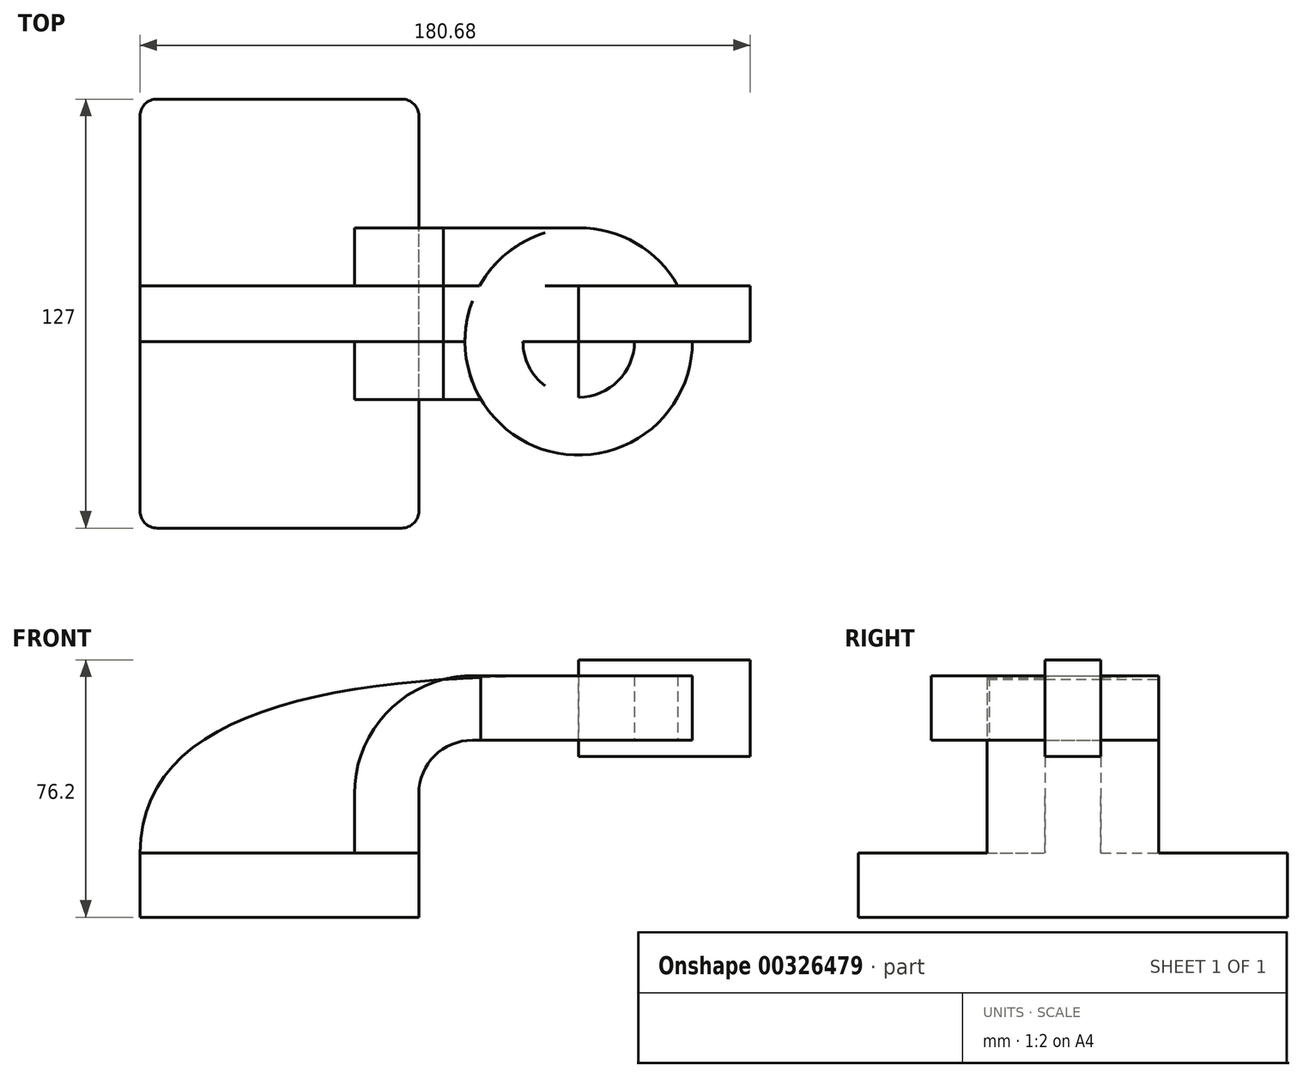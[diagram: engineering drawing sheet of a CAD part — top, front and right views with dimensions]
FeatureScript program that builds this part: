
annotation { "Feature Type Name" : "Feature", "Feature Type Description" : "" }
export const myFeature = defineFeature(function(context is Context, id is Id, definition is map)
    precondition{}
    {
        {
            var Q0;
            Q0=qCreatedBy(makeId("Front.planeOp"),FACE);
            var sketch = newSketch(context, id + "F0", { "sketchPlane" : qUnion([Q0])});
            skLineSegment(sketch, "E0.bottom", {"start": v(-41.28, 9.52) * mm, "end": v(41.27, 9.53) * mm});
            skLineSegment(sketch, "E0.top", {"start": v(-41.28, -9.52) * mm, "end": v(41.28, -9.52) * mm});
            skLineSegment(sketch, "E0.left", {"start": v(-41.28, 9.52) * mm, "end": v(-41.28, -9.53) * mm});
            skLineSegment(sketch, "E0.right", {"start": v(41.27, 9.53) * mm, "end": v(41.28, -9.52) * mm});
            skPoint(sketch, "E0.middle", {"position": v(0, 0) * mm});
            skLineSegment(sketch, "E1.bottom", {"start": v(88.6, 38.1) * mm, "end": v(139.4, 38.1) * mm});
            skLineSegment(sketch, "E1.top", {"start": v(88.6, 66.68) * mm, "end": v(139.4, 66.68) * mm});
            skLineSegment(sketch, "E1.left", {"start": v(88.6, 38.1) * mm, "end": v(88.6, 66.68) * mm});
            skLineSegment(sketch, "E1.right", {"start": v(139.4, 38.1) * mm, "end": v(139.4, 66.68) * mm});
            skPoint(sketch, "E1.middle", {"position": v(114, 52.39) * mm});
            skLineSegment(sketch, "E2", {"start": v(41.27, 9.53) * mm, "end": v(41.27, 27) * mm});
            skArc(sketch, "E3", {"start": v(41.27, 27) * mm, "mid": v(45.92, 38.23) * mm, "end": v(57.15, 42.88) * mm});
            skLineSegment(sketch, "E4", {"start": v(57.15, 42.88) * mm, "end": v(113.89, 42.88) * mm});
            skLineSegment(sketch, "E5.0", {"start": v(57.15, 61.93) * mm, "end": v(113.89, 61.93) * mm});
            skArc(sketch, "E5.1", {"start": v(22.22, 27) * mm, "mid": v(32.45, 51.7) * mm, "end": v(57.15, 61.93) * mm});
            skLineSegment(sketch, "E5.2", {"start": v(22.22, 9.53) * mm, "end": v(22.22, 27) * mm});
            skLineSegment(sketch, "E6", {"start": v(113.89, 61.93) * mm, "end": v(114, 52.39) * mm});
            skLineSegment(sketch, "E7", {"start": v(114.28, 53.8) * mm, "end": v(113.89, 42.88) * mm});
            skFitSpline(sketch, "E8", {"points": [v(88.6, 61.93) * mm, v(-41.28, 9.52) * mm], "startDerivative": vector(-223.24, 1.61) * mm, "endDerivative": vector(-0.87, -125.7) * mm});
            skSolve(sketch);
        }
        {
            var Q0;
            Q0=makeQuery(id+"F0.imprint","IMPRINT",FACE,{"disambiguationData":[TD([[makeQuery(id+"F0.imprint","IMPRINT",EDGE,{"derivedFrom":sQuery(id+"F0.wireOp",EDGE,"E0.top")}),1.0]])]});
            extrude(context, id + "F1", {"entities" : qUnion([Q0]), "endBound" : BoundingType.SYMMETRIC, "depth" : 127 * mm});
        }
        {
            var Q0;
            {var subQ1=sQuery(id+"F0.wireOp",EDGE,"E2");Q0=makeQuery(id+"F0.imprint","IMPRINT",FACE,{"disambiguationData":[TD([[makeQuery(id+"F0.imprint","IMPRINT",EDGE,{"derivedFrom":subQ1}),1.0]])]});}
            extrude(context, id + "F2", {"entities" : qUnion([Q0]), "operationType" : NewBodyOperationType.ADD, "endBound" : BoundingType.SYMMETRIC, "depth" : 50.8 * mm});
        }
        {
            var Q0;
            Q0 = qSketchRegion(id + "F0", true);
            extrude(context, id + "F3", {"entities" : qUnion([Q0]), "operationType" : NewBodyOperationType.ADD, "endBound" : BoundingType.SYMMETRIC, "depth" : 16.5 * mm});
        }
        {
            var Q0;
            {var subQ0=sQuery(id+"F0.wireOp",EDGE,"E8");var subQ1=sQuery(id+"F0.wireOp",EDGE,"E5.1");var subQ2=sQuery(id+"F0.wireOp",EDGE,"E5.0");var subQ3=sQuery(id+"F0.wireOp",EDGE,"E4");var subQ4=sQuery(id+"F0.wireOp",EDGE,"E3");var subQ5=sQuery(id+"F0.wireOp",EDGE,"E2");var subQ6=sQuery(id+"F0.wireOp",EDGE,"E1.left");Q0=makeQuery(id+"F3.boolean.opBoolean","SPLIT",FACE,{"disambiguationData":[TD([makeQuery(id+"F2.opExtrude","CAP_FACE",FACE,{"disambiguationData":[OSD([sQuery(id+"F0.wireOp",EDGE,"E0.bottom"),subQ6,subQ5,subQ4,subQ3,subQ2,subQ1,sQuery(id+"F0.wireOp",EDGE,"E5.2"),subQ0])],"isStart":true})])],"derivedFrom":makeQuery(id+"F2.opExtrude","SWEPT_FACE",FACE,{"disambiguationData":[OSD([subQ6])]})});}
            var Q1;
            {var subQ0=sQuery(id+"F0.wireOp",EDGE,"E1.left");Q1=makeQuery(id+"F3.boolean.opBoolean","INTERSECT",EDGE,{"derivedFrom":[makeQuery(id+"F2.opExtrude","SWEPT_FACE",FACE,{"disambiguationData":[OSD([subQ0])]}),makeQuery(id+"F3.opExtrude","CAP_FACE",FACE,{"disambiguationData":[OSD([sQuery(id+"F0.wireOp",EDGE,"E0.top"),sQuery(id+"F0.wireOp",EDGE,"E0.left"),sQuery(id+"F0.wireOp",EDGE,"E0.right"),sQuery(id+"F0.wireOp",EDGE,"E1.bottom"),sQuery(id+"F0.wireOp",EDGE,"E1.top"),subQ0,sQuery(id+"F0.wireOp",EDGE,"E1.right"),sQuery(id+"F0.wireOp",EDGE,"E2"),sQuery(id+"F0.wireOp",EDGE,"E3"),sQuery(id+"F0.wireOp",EDGE,"E4"),sQuery(id+"F0.wireOp",EDGE,"E5.0"),sQuery(id+"F0.wireOp",EDGE,"E5.1"),sQuery(id+"F0.wireOp",EDGE,"E8")])],"isStart":false})]});}
            revolve(context, id + "F4", {"operationType" : NewBodyOperationType.ADD, "entities" : qUnion([Q0]), "axis" : qUnion([Q1]), "revolveType" : RevolveType.FULL});
        }
        {
            var Q0;
            Q0=makeQuery(id+"F1.opExtrude","CAP_EDGE",EDGE,{"disambiguationData":[OSD([sQuery(id+"F0.wireOp",EDGE,"E0.left")])],"isStart":false});
            var Q1;
            Q1=makeQuery(id+"F1.opExtrude","CAP_EDGE",EDGE,{"disambiguationData":[OSD([sQuery(id+"F0.wireOp",EDGE,"E0.right")])],"isStart":false});
            var Q2;
            Q2=makeQuery(id+"F1.opExtrude","CAP_EDGE",EDGE,{"disambiguationData":[OSD([sQuery(id+"F0.wireOp",EDGE,"E0.right")])],"isStart":true});
            var Q3;
            Q3=makeQuery(id+"F1.opExtrude","CAP_EDGE",EDGE,{"disambiguationData":[OSD([sQuery(id+"F0.wireOp",EDGE,"E0.left")])],"isStart":true});
            fillet(context, id + "F5", {"entities" : qUnion([Q0, Q1, Q2, Q3]), "radius" : 5.08 * mm, "tangentPropagation" : true, "allowEdgeOverflow" : false});
        }
    });
